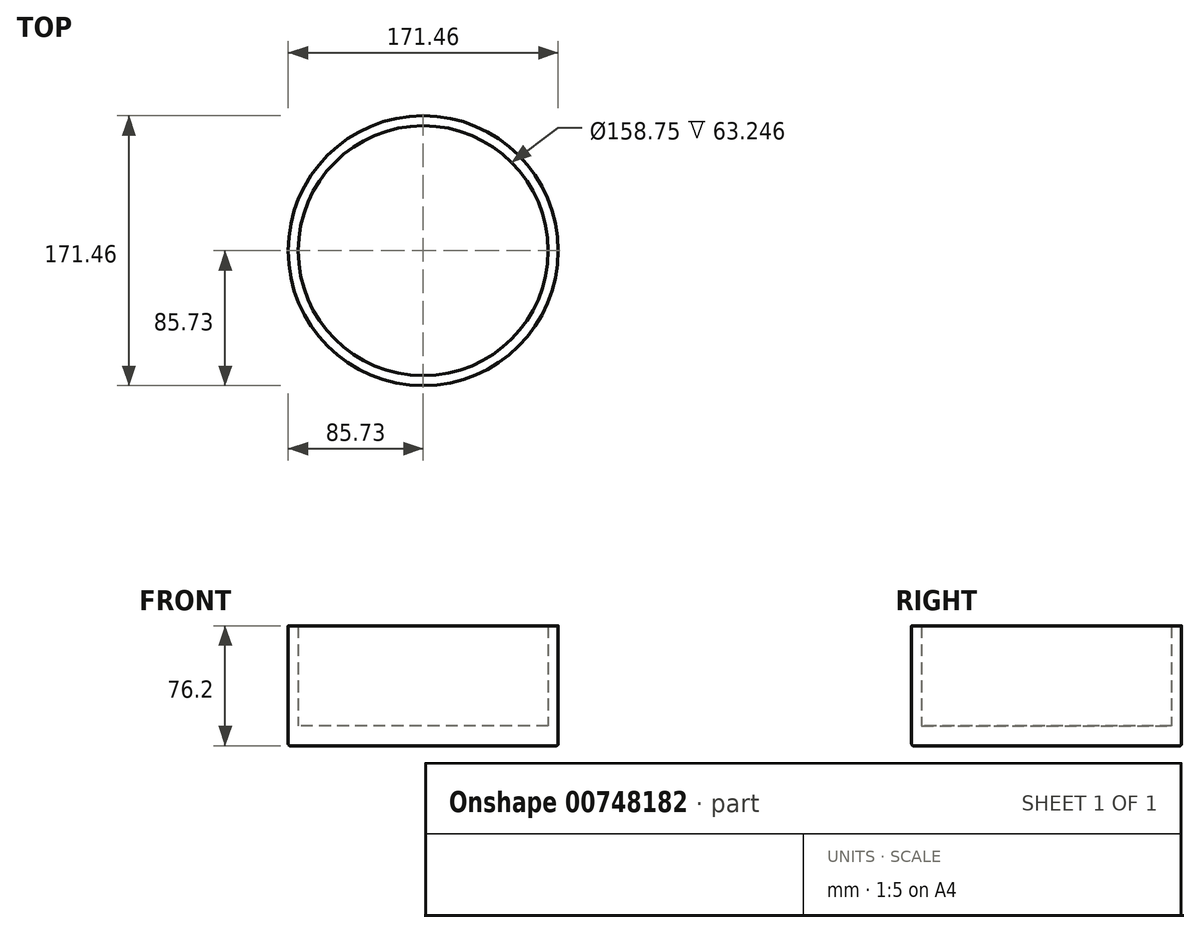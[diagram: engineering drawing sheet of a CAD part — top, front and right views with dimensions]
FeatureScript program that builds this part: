
annotation { "Feature Type Name" : "Feature", "Feature Type Description" : "" }
export const myFeature = defineFeature(function(context is Context, id is Id, definition is map)
    precondition{}
    {
        {
            var Q0;
            Q0=qCreatedBy(makeId("Top.planeOp"),FACE);
            var sketch = newSketch(context, id + "F0", { "sketchPlane" : qUnion([Q0])});
            skCircle(sketch, "E0", {"center": v(0, 0) * mm, "radius": 85.73 * mm});
            skCircle(sketch, "E1", {"center": v(0, 0) * mm, "radius": 79.38 * mm});
            skSolve(sketch);
        }
        {
            var Q0;
            Q0=makeQuery(id+"F0.imprint","IMPRINT",FACE,{"disambiguationData":[TD([[makeQuery(id+"F0.imprint","IMPRINT",EDGE,{"derivedFrom":sQuery(id+"F0.wireOp",EDGE,"E1")}),1.0]])]});
            extrude(context, id + "F1", {"entities" : qUnion([Q0]), "depth" : 12.7 * mm, "offsetDistance" : 25.4 * mm});
        }
        {
            var Q0;
            Q0 = qSketchRegion(id + "F0", true);
            extrude(context, id + "F2", {"entities" : qUnion([Q0]), "operationType" : NewBodyOperationType.ADD, "depth" : 76.2 * mm, "offsetDistance" : 25.4 * mm});
        }
        {
            var Q0;
            Q0=makeQuery(id+"F2.opExtrude","CAP_EDGE",EDGE,{"disambiguationData":[OSD([sQuery(id+"F0.wireOp",EDGE,"E0")])],"isStart":true});
            var Q1;
            Q1=makeQuery(id+"F1.opExtrude","CAP_EDGE",EDGE,{"disambiguationData":[OSD([sQuery(id+"F0.wireOp",EDGE,"E1")])],"isStart":false});
            fillet(context, id + "F3", {"entities" : qUnion([Q0, Q1]), "radius" : 1.27 * mm, "tangentPropagation" : true, "allowEdgeOverflow" : false});
        }
        {
            var Q0;
            Q0=makeQuery(id+"F2.opExtrude","CAP_EDGE",EDGE,{"disambiguationData":[OSD([sQuery(id+"F0.wireOp",EDGE,"E1")])],"isStart":false});
            var Q1;
            Q1=makeQuery(id+"F2.opExtrude","CAP_EDGE",EDGE,{"disambiguationData":[OSD([sQuery(id+"F0.wireOp",EDGE,"E0")])],"isStart":false});
            fillet(context, id + "F4", {"entities" : qUnion([Q0, Q1]), "radius" : 0.25 * mm, "tangentPropagation" : true, "allowEdgeOverflow" : false});
        }
    });
